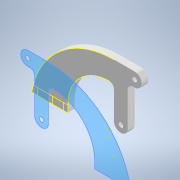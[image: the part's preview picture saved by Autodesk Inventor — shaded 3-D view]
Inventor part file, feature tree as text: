
AUTODESK INVENTOR PART (.ipt)
format: ipt  version: 2020 (Build 240168000, 168)  size: 224,768 bytes
history: native  units: in
note: dims shown in document units (in); Inventor stores cm internally (conversion verified against a paired STEP export)
features: reference x9, extrude x6, sketch x6, other x2, projected_geometry x1
ambient origin geometry x8: Origin, YZ Plane, XZ Plane, XY Plane, X Axis, Y Axis, Z Axis, Center Point
bodies: Solid1 (feature_tree)
feature tree (24):
  extrude  "Extrusion1"  Depth=0.2437in
  extrude  "Extrusion2"  Depth=0.0787in
  extrude  "Extrusion3"  Depth=0.1181in
  extrude  "Extrusion4"  Depth=0.2362in
  extrude  "Extrusion5"  Depth=0.0787in
  extrude  "Extrusion6"  Depth=0.2362in
  sketch  "Sketch1"  dims[d0=1.4173in d1=0.2437in]
  sketch  "Sketch2"  dims[d2=0.0787in d3=2.8496in]
  reference  "Reference4"
  reference  "Reference5"
  reference  "Reference6"
  reference  "Reference7"
  reference  "Reference8"
  reference  "Reference9"
  reference  "Reference10"
  reference  "Reference11"
  reference  "Reference12"
  sketch  "Sketch4"  dims[d11=1.1811in d14=0.1181in]
  sketch  "Sketch5"  dims[d17=0.0787in d18=0.2362in]
  sketch  "Sketch6"  dims[d19=0.1181in d20=0.0787in]
  sketch  "Sketch8"  dims[d21=0.3543in d23=0.2362in d24=0.7087in d25=0.0787in d26=0.0787in d27=0.0787in d28=0.0787in d31=0.0787in d34=0.1181in d35=0.0in d36=0.3681in d37=0.0in d38=0.1181in d39=0.0in d40=0.0392in d41=0.0787in d42=0.1181in d43=0.0in d44=0.0394in d45=0.2362in d46=0.1181in d47=0.0in d48=0.0787in d49=0.1181in d50=0.1772in d51=0.1181in d52=0.0787in d53=0.1181in d54=0.1772in d55=0.1181in d56=0.0787in d57=0.1181in d58=0.0in]
  projected_geometry  "Projected Loop2"
  other  "Assembly1"
  other  "Horn:1"
